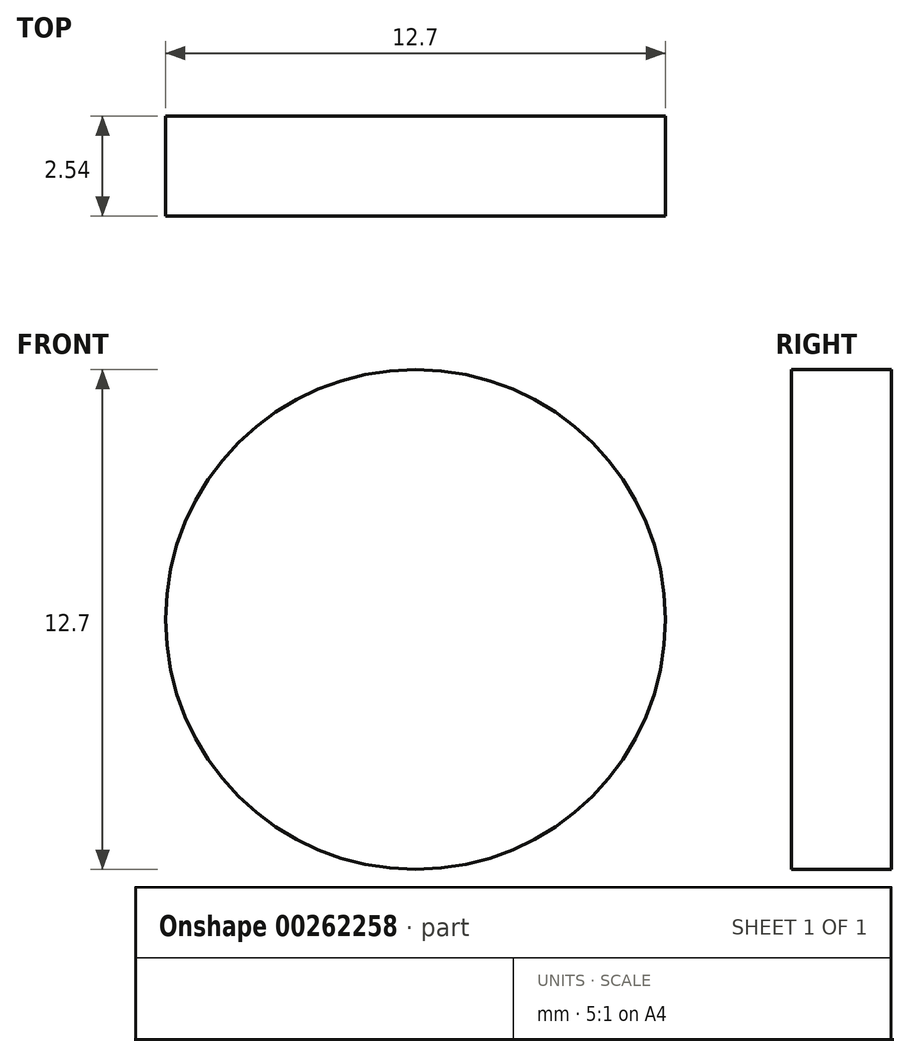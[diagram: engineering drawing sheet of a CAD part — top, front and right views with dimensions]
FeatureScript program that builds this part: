
annotation { "Feature Type Name" : "Feature", "Feature Type Description" : "" }
export const myFeature = defineFeature(function(context is Context, id is Id, definition is map)
    precondition{}
    {
        {
            var Q0;
            Q0=qCreatedBy(makeId("Front.planeOp"),FACE);
            var sketch = newSketch(context, id + "F0", { "sketchPlane" : qUnion([Q0])});
            skCircle(sketch, "E0", {"center": v(0, 0) * mm, "radius": 6.35 * mm});
            skSolve(sketch);
        }
        {
            var Q0;
            Q0 = qSketchRegion(id + "F0", true);
            extrude(context, id + "F1", {"entities" : qUnion([Q0]), "depth" : 2.54 * mm});
        }
    });
